# Revit family: Manifold_FLND-JCI_Sapphire_Plus-(70bar)Novec1230
name_source: partatom
category: Specialty Equipment
revit_build: Autodesk Revit 2017 (Build: 20171027_0315(x64)
units: mm (PartAtom-declared; Revit-internal decimal feet)

## family parameters
Always vertical = No
Cut with Voids When Loaded = No
OmniClass Number = 23.29.33.13.11
Part Type = Normal
Room Calculation Point = No
Round Connector Dimension = Use Diameter
Shared = No
Work Plane-Based = Yes

## types (9) — shared parameters
Date Modified = YYYY/MM/DD
Diameter = 47.6 mm  [stored 0.156168 ft]
Family Version = 1.1
Fire Suppression Agent = 3M Novec'' 1230 Fire Protection Fluid
Height = 41 mm  [stored 0.134514 ft]
Length = 47.6 mm  [stored 0.156168 ft]
Manufacturer = Johnson Controls, Inc.
Material = JCI - Metal - Stainless Steel - Satin
Model Disclaimer = For More Information Contact JOHNSON CONTROLS
Operating Temperature = 122 °F
Pipe Diameter = 12.7 mm  [stored 0.0416667 ft]
Product Documentation Link = http://www.sapphireplus.com
Product Material = JCI - Metal - Stainless Steel - Satin
Product Page URL = http://www.sapphireplus.com
Unit Assembly = Sapphire Plus_Manifold 150Dia
Width = 47.6 mm  [stored 0.156168 ft]
zero-valued in all types: Default Elevation

## per-type parameters (varying)
| type | Description | Model | Port No | Port Type | URL | Weight |
| 150mm_FLND_2PT |  |  | Manifold : 2 PT | 2 | http://www.sapphireplus.com | 0.00 lbf |
| 150mm_FLND_3PT | 150mm_FLND_3PT | 307700014 | Manifold : 3 PT | 3 | http://www.sapphireplus.com | 388.00 lbf |
| 150mm_FLND_4PT | 150mm_FLND_4PT | 307700015 | Manifold : 4 PT | 4 | http://www.sapphireplus.com | 435.30 lbf |
| 150mm_FLND_5PT | 150mm_FLND_5PT | 307700016 | Manifold : 5 PT | 5 | http://www.sapphireplus.com | 727.50 lbf |
| 150mm_FLND_6PT | 150mm_FLND_6PT | 307700017 | Manifold : 6 PT | 6 | http://www.sapphireplus.com | 776.00 lbf |
| 150mm_FLND_7PT | 150mm_FLND_7PT | 307700018 | Manifold : 7 PT | 7 | http://www.sapphireplus.com | 823.40 lbf |
| 150mm_FLND_8PT | 150mm_FLND_8PT | 307700019 | Manifold : 8 PT | 8 | http://www.sapphireplus.com | 870.80 lbf |
| 150mm_FLND_9PT | 150mm_FLND_9PT | 307700020 | Manifold : 9 PT | 9 | http://www.sapphireplus.com | 1164.00 lbf |
| 150mm_FLND_10PT | 150mm_FLND_10PT | 307700021 | Manifold : 10 PT | 10 | https://www.ansul.com | 1211.40 lbf |

note: [stored X ft] marks values corroborated as IEEE doubles in the binary element streams (Revit-internal decimal feet)

## geometry (parser evidence)
native form markers: Sweep x9
no freeform markers — native parametric forms only
